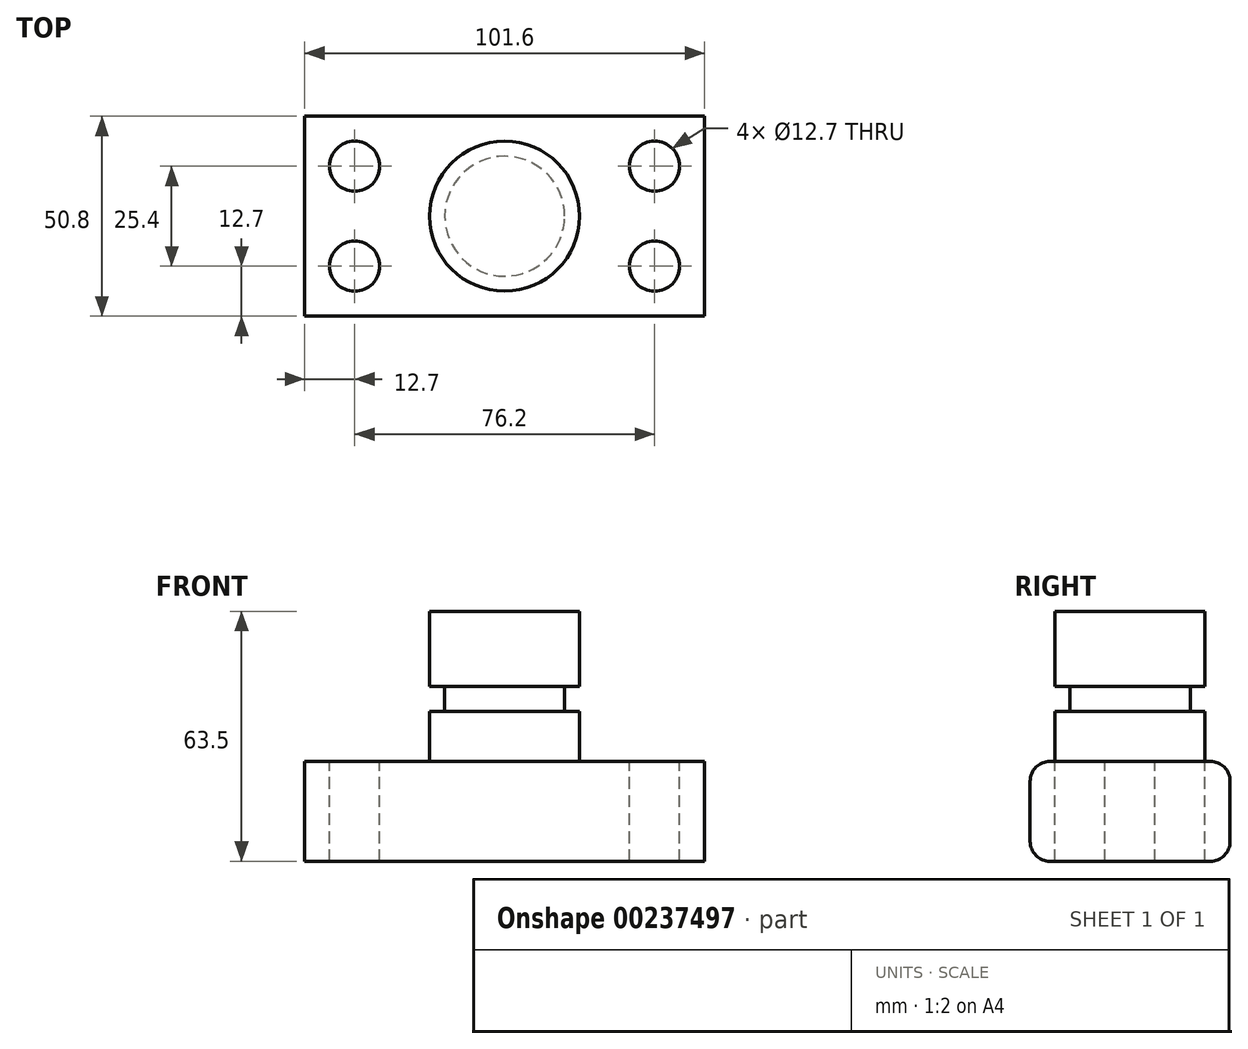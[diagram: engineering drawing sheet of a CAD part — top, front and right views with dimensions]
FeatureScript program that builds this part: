
annotation { "Feature Type Name" : "Feature", "Feature Type Description" : "" }
export const myFeature = defineFeature(function(context is Context, id is Id, definition is map)
    precondition{}
    {
        {
            var Q0;
            Q0=qCreatedBy(makeId("Top.planeOp"),FACE);
            var sketch = newSketch(context, id + "F0", { "sketchPlane" : qUnion([Q0])});
            skLineSegment(sketch, "E0.bottom", {"start": v(50.8, 25.4) * mm, "end": v(-50.8, 25.4) * mm});
            skLineSegment(sketch, "E0.top", {"start": v(50.8, -25.4) * mm, "end": v(-50.8, -25.4) * mm});
            skLineSegment(sketch, "E0.left", {"start": v(50.8, 25.4) * mm, "end": v(50.8, -25.4) * mm});
            skLineSegment(sketch, "E0.right", {"start": v(-50.8, 25.4) * mm, "end": v(-50.8, -25.4) * mm});
            skPoint(sketch, "E0.middle", {"position": v(0, 0) * mm});
            skSolve(sketch);
        }
        {
            var Q0;
            Q0 = qSketchRegion(id + "F0", true);
            extrude(context, id + "F1", {"entities" : qUnion([Q0]), "depth" : 25.4 * mm});
        }
        {
            var Q0;
            Q0=makeQuery(id+"F1.opExtrude","CAP_FACE",FACE,{"disambiguationData":[OSD([sQuery(id+"F0.wireOp",EDGE,"E0.bottom"),sQuery(id+"F0.wireOp",EDGE,"E0.top"),sQuery(id+"F0.wireOp",EDGE,"E0.left"),sQuery(id+"F0.wireOp",EDGE,"E0.right")])],"isStart":false});
            var sketch = newSketch(context, id + "F2", { "sketchPlane" : qUnion([Q0])});
            skCircle(sketch, "E1", {"center": v(-38.1, 12.7) * mm, "radius": 6.35 * mm});
            skCircle(sketch, "E2", {"center": v(38.1, 12.7) * mm, "radius": 6.35 * mm});
            skCircle(sketch, "E3", {"center": v(-38.1, -12.7) * mm, "radius": 6.35 * mm});
            skCircle(sketch, "E4", {"center": v(38.1, -12.7) * mm, "radius": 6.35 * mm});
            skSolve(sketch);
        }
        {
            var Q0;
            Q0 = qSketchRegion(id + "F2", true);
            extrude(context, id + "F3", {"entities" : qUnion([Q0]), "operationType" : NewBodyOperationType.REMOVE, "endBound" : BoundingType.THROUGH_ALL, "oppositeDirection" : true, "depth" : 25.4 * mm});
        }
        {
            var Q0;
            Q0=qCreatedBy(makeId("Front.planeOp"),FACE);
            var sketch = newSketch(context, id + "F4", { "sketchPlane" : qUnion([Q0])});
            skLineSegment(sketch, "E5.bottom", {"start": v(0, 25.4) * mm, "end": v(-19.05, 25.4) * mm});
            skLineSegment(sketch, "E5.top", {"start": v(0, 63.5) * mm, "end": v(-19.05, 63.5) * mm});
            skLineSegment(sketch, "E5.left", {"start": v(0, 25.4) * mm, "end": v(0, 63.5) * mm});
            skLineSegment(sketch, "E5.right", {"start": v(-19.05, 25.4) * mm, "end": v(-19.05, 63.5) * mm});
            skSolve(sketch);
        }
        {
            var Q0;
            Q0=makeQuery(id+"F4.imprint","IMPRINT",FACE,{"disambiguationData":[TD([[makeQuery(id+"F4.imprint","IMPRINT",EDGE,{"derivedFrom":sQuery(id+"F4.wireOp",EDGE,"E5.bottom")}),-1.0]])]});
            var Q1;
            Q1=sQuery(id+"F4.wireOp",EDGE,"E5.left");
            revolve(context, id + "F5", {"operationType" : NewBodyOperationType.ADD, "entities" : qUnion([Q0]), "axis" : qUnion([Q1]), "revolveType" : RevolveType.FULL});
        }
        {
            var Q0;
            {var subQ0=sQuery(id+"F0.wireOp",EDGE,"E0.right");var subQ1=sQuery(id+"F0.wireOp",EDGE,"E0.top");Q0=makeQuery(id+"F5.boolean.opBoolean","SPLIT",EDGE,{"disambiguationData":[TD([makeQuery(id+"F1.opExtrude","SWEPT_FACE",FACE,{"disambiguationData":[OSD([subQ0])]})])],"derivedFrom":makeQuery(id+"F1.opExtrude","CAP_EDGE",EDGE,{"disambiguationData":[OSD([subQ1])],"isStart":false})});}
            var Q1;
            {var subQ0=sQuery(id+"F0.wireOp",EDGE,"E0.left");var subQ1=sQuery(id+"F0.wireOp",EDGE,"E0.top");Q1=makeQuery(id+"F5.boolean.opBoolean","SPLIT",EDGE,{"disambiguationData":[TD([makeQuery(id+"F1.opExtrude","SWEPT_FACE",FACE,{"disambiguationData":[OSD([subQ0])]})])],"derivedFrom":makeQuery(id+"F1.opExtrude","CAP_EDGE",EDGE,{"disambiguationData":[OSD([subQ1])],"isStart":false})});}
            var Q2;
            Q2=makeQuery(id+"F1.opExtrude","CAP_EDGE",EDGE,{"disambiguationData":[OSD([sQuery(id+"F0.wireOp",EDGE,"E0.top")])],"isStart":true});
            var Q3;
            {var subQ0=sQuery(id+"F0.wireOp",EDGE,"E0.bottom");var subQ1=sQuery(id+"F0.wireOp",EDGE,"E0.left");Q3=makeQuery(id+"F5.boolean.opBoolean","SPLIT",EDGE,{"disambiguationData":[TD([makeQuery(id+"F1.opExtrude","SWEPT_FACE",FACE,{"disambiguationData":[OSD([subQ1])]})])],"derivedFrom":makeQuery(id+"F1.opExtrude","CAP_EDGE",EDGE,{"disambiguationData":[OSD([subQ0])],"isStart":false})});}
            var Q4;
            {var subQ0=sQuery(id+"F0.wireOp",EDGE,"E0.bottom");var subQ1=sQuery(id+"F0.wireOp",EDGE,"E0.right");Q4=makeQuery(id+"F5.boolean.opBoolean","SPLIT",EDGE,{"disambiguationData":[TD([makeQuery(id+"F1.opExtrude","SWEPT_FACE",FACE,{"disambiguationData":[OSD([subQ1])]})])],"derivedFrom":makeQuery(id+"F1.opExtrude","CAP_EDGE",EDGE,{"disambiguationData":[OSD([subQ0])],"isStart":false})});}
            var Q5;
            Q5=makeQuery(id+"F1.opExtrude","CAP_EDGE",EDGE,{"disambiguationData":[OSD([sQuery(id+"F0.wireOp",EDGE,"E0.bottom")])],"isStart":true});
            fillet(context, id + "F6", {"entities" : qUnion([Q0, Q1, Q2, Q3, Q4, Q5]), "radius" : 5.08 * mm, "tangentPropagation" : true, "allowEdgeOverflow" : false});
        }
        {
            var Q0;
            Q0=qCreatedBy(makeId("Front.planeOp"),FACE);
            var sketch = newSketch(context, id + "F7", { "sketchPlane" : qUnion([Q0])});
            skLineSegment(sketch, "E6.bottom", {"start": v(-22.96, 44.45) * mm, "end": v(-15.24, 44.45) * mm});
            skLineSegment(sketch, "E6.top", {"start": v(-22.96, 38.1) * mm, "end": v(-15.24, 38.1) * mm});
            skLineSegment(sketch, "E6.left", {"start": v(-22.96, 44.45) * mm, "end": v(-22.96, 38.1) * mm});
            skLineSegment(sketch, "E6.right", {"start": v(-15.24, 44.45) * mm, "end": v(-15.24, 38.1) * mm});
            skSolve(sketch);
        }
        {
            var Q0;
            Q0 = qSketchRegion(id + "F7", true);
            var Q1;
            Q1=makeQuery(id+"F5.opRevolve","SWEPT_FACE",FACE,{"disambiguationData":[OSD([sQuery(id+"F4.wireOp",EDGE,"E5.right")])]});
            revolve(context, id + "F8", {"operationType" : NewBodyOperationType.REMOVE, "entities" : qUnion([Q0]), "axis" : qUnion([Q1]), "revolveType" : RevolveType.FULL, "oppositeDirection" : true});
        }
    });
